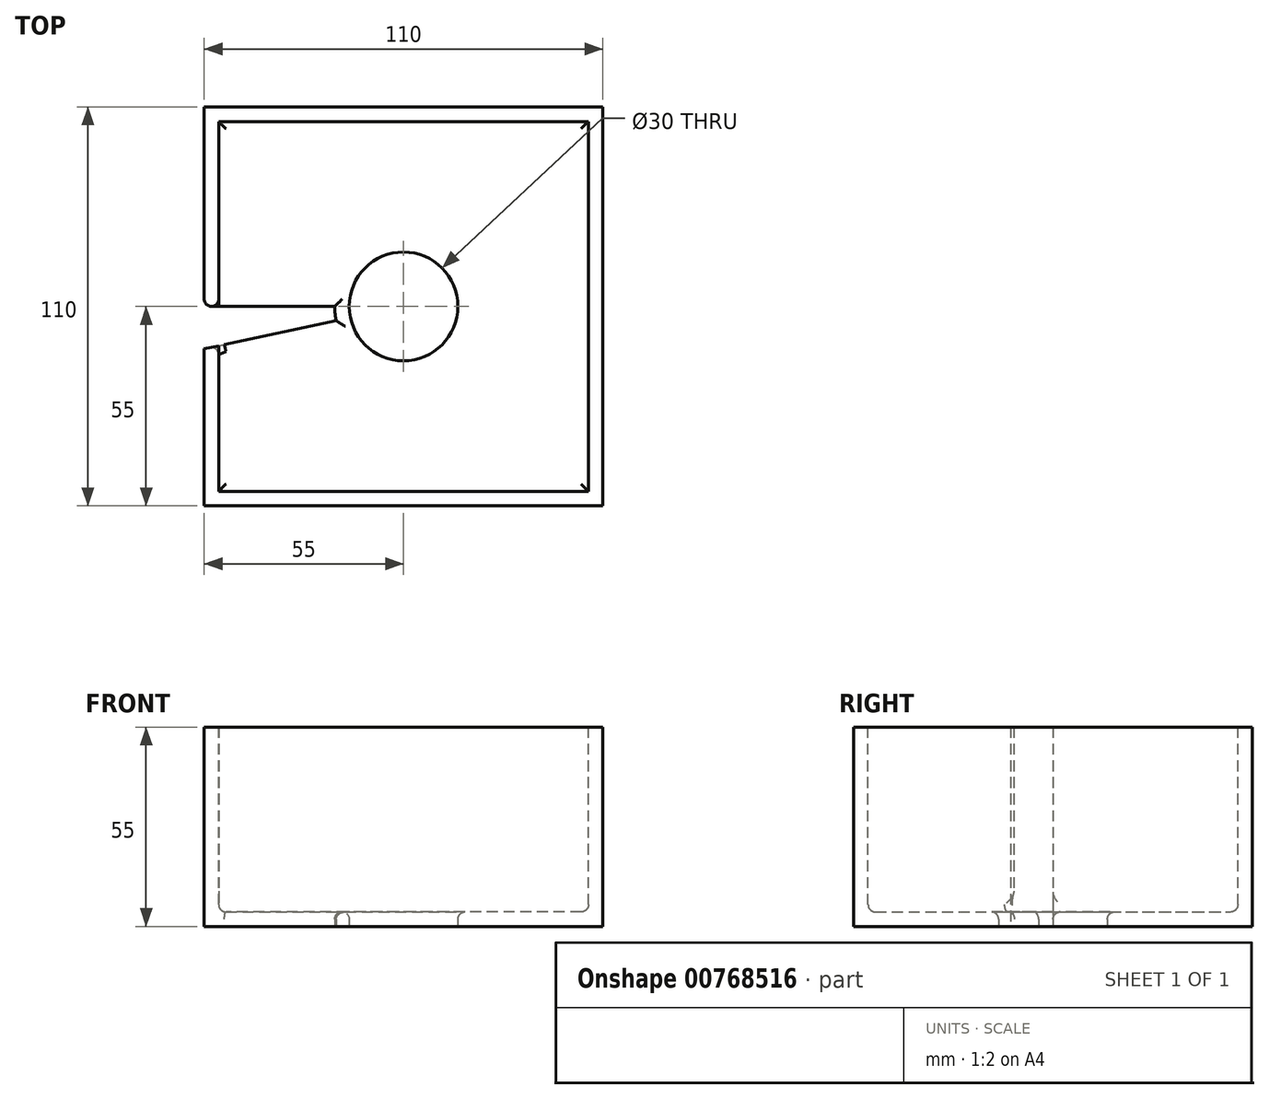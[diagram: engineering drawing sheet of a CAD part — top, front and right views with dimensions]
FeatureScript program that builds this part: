
annotation { "Feature Type Name" : "Feature", "Feature Type Description" : "" }
export const myFeature = defineFeature(function(context is Context, id is Id, definition is map)
    precondition{}
    {
        {
            var Q0;
            Q0=qCreatedBy(makeId("Top.planeOp"),FACE);
            var sketch = newSketch(context, id + "F0", { "sketchPlane" : qUnion([Q0])});
            skLineSegment(sketch, "E0.bottom", {"start": v(55, 55) * mm, "end": v(-55, 55) * mm});
            skLineSegment(sketch, "E0.top", {"start": v(55, -55) * mm, "end": v(-55, -55) * mm});
            skLineSegment(sketch, "E0.left", {"start": v(55, 55) * mm, "end": v(55, -55) * mm});
            skLineSegment(sketch, "E0.right", {"start": v(-55, 55) * mm, "end": v(-55, -55) * mm});
            skPoint(sketch, "E0.middle", {"position": v(0, 0) * mm});
            skSolve(sketch);
        }
        {
            var Q0;
            Q0 = qSketchRegion(id + "F0", true);
            extrude(context, id + "F1", {"entities" : qUnion([Q0]), "depth" : (110 / 2) * mm, "offsetDistance" : 25 * mm});
        }
        {
            var Q0;
            Q0=makeQuery(id+"F1.opExtrude","CAP_FACE",FACE,{"disambiguationData":[OSD([sQuery(id+"F0.wireOp",EDGE,"E0.bottom"),sQuery(id+"F0.wireOp",EDGE,"E0.top"),sQuery(id+"F0.wireOp",EDGE,"E0.left"),sQuery(id+"F0.wireOp",EDGE,"E0.right")])],"isStart":false});
            var sketch = newSketch(context, id + "F2", { "sketchPlane" : qUnion([Q0])});
            skLineSegment(sketch, "E1.bottom", {"start": v(51, -51) * mm, "end": v(-51, -51) * mm});
            skLineSegment(sketch, "E1.top", {"start": v(51, 51) * mm, "end": v(-51, 51) * mm});
            skLineSegment(sketch, "E1.left", {"start": v(51, -51) * mm, "end": v(51, 51) * mm});
            skLineSegment(sketch, "E1.right", {"start": v(-51, -51) * mm, "end": v(-51, 51) * mm});
            skPoint(sketch, "E1.middle", {"position": v(0, 0) * mm});
            skSolve(sketch);
        }
        {
            var Q0;
            Q0 = qSketchRegion(id + "F2", true);
            extrude(context, id + "F3", {"entities" : qUnion([Q0]), "operationType" : NewBodyOperationType.REMOVE, "oppositeDirection" : true, "depth" : ((110 / 2) - 4) * mm, "offsetDistance" : 25 * mm});
        }
        {
            var Q0;
            Q0=makeQuery(id+"F1.opExtrude","CAP_FACE",FACE,{"disambiguationData":[OSD([sQuery(id+"F0.wireOp",EDGE,"E0.bottom"),sQuery(id+"F0.wireOp",EDGE,"E0.top"),sQuery(id+"F0.wireOp",EDGE,"E0.left"),sQuery(id+"F0.wireOp",EDGE,"E0.right")])],"isStart":true});
            var sketch = newSketch(context, id + "F4", { "sketchPlane" : qUnion([Q0])});
            skPoint(sketch, "E2.endSnap0", {"position": v(-55, 0) * mm});
            skLineSegment(sketch, "E3", {"start": v(-19, 0) * mm, "end": v(-85, 0) * mm});
            skLineSegment(sketch, "E4", {"start": v(-18.58, 3.95) * mm, "end": v(-83.14, 17.67) * mm});
            skArc(sketch, "E5", {"start": v(-19, 0) * mm, "mid": v(-18.9, 1.99) * mm, "end": v(-18.58, 3.95) * mm});
            skArc(sketch, "E6", {"start": v(-85, 0) * mm, "mid": v(-84.53, 8.88) * mm, "end": v(-83.14, 17.67) * mm});
            skSolve(sketch);
        }
        {
            var Q0;
            Q0 = qSketchRegion(id + "F4", true);
            extrude(context, id + "F5", {"entities" : qUnion([Q0]), "operationType" : NewBodyOperationType.REMOVE, "endBound" : BoundingType.THROUGH_ALL, "oppositeDirection" : true, "depth" : 25 * mm, "offsetDistance" : 25 * mm});
        }
        {
            var Q0;
            Q0=qCreatedBy(makeId("Right.planeOp"),FACE);
            var sketch = newSketch(context, id + "F6", { "sketchPlane" : qUnion([Q0])});
            skLineSegment(sketch, "E7", {"start": v(0, -32.4) * mm, "end": v(0, 66.47) * mm});
            skSolve(sketch);
        }
        {
            var Q0;
            Q0=makeQuery(id+"F1.opExtrude","CAP_FACE",FACE,{"disambiguationData":[OSD([sQuery(id+"F0.wireOp",EDGE,"E0.bottom"),sQuery(id+"F0.wireOp",EDGE,"E0.top"),sQuery(id+"F0.wireOp",EDGE,"E0.left"),sQuery(id+"F0.wireOp",EDGE,"E0.right")])],"isStart":true});
            var sketch = newSketch(context, id + "F7", { "sketchPlane" : qUnion([Q0])});
            skCircle(sketch, "E8", {"center": v(0, 0) * mm, "radius": 15 * mm});
            skSolve(sketch);
        }
        {
            var Q0;
            Q0 = qSketchRegion(id + "F7", true);
            extrude(context, id + "F8", {"entities" : qUnion([Q0]), "operationType" : NewBodyOperationType.REMOVE, "endBound" : BoundingType.THROUGH_ALL, "oppositeDirection" : true, "depth" : 25 * mm, "offsetDistance" : 25 * mm});
        }
        {
            var Q0;
            Q0=makeQuery(id+"Fbr1V4HkgtgxKTV_1.12.F5.boolean.opBoolean","INTERSECT",EDGE,{"derivedFrom":[makeQuery(id+"F3.boolean.opBoolean","COPY",FACE,{"derivedFrom":makeQuery(id+"F3.opExtrude","CAP_FACE",FACE,{"disambiguationData":[OSD([sQuery(id+"F2.wireOp",EDGE,"E1.bottom"),sQuery(id+"F2.wireOp",EDGE,"E1.top"),sQuery(id+"F2.wireOp",EDGE,"E1.left"),sQuery(id+"F2.wireOp",EDGE,"E1.right")])],"isStart":false})}),makeQuery(id+"Fbr1V4HkgtgxKTV_1.12.F5.opExtrude","SWEPT_FACE",FACE,{"disambiguationData":[OSD([sQuery(id+"F4.wireOp",EDGE,"E4")])]})]});
            var Q1;
            Q1=makeQuery(id+"Fbr1V4HkgtgxKTV_1.13.F5.boolean.opBoolean","INTERSECT",EDGE,{"derivedFrom":[makeQuery(id+"F3.boolean.opBoolean","COPY",FACE,{"derivedFrom":makeQuery(id+"F3.opExtrude","CAP_FACE",FACE,{"disambiguationData":[OSD([sQuery(id+"F2.wireOp",EDGE,"E1.bottom"),sQuery(id+"F2.wireOp",EDGE,"E1.top"),sQuery(id+"F2.wireOp",EDGE,"E1.left"),sQuery(id+"F2.wireOp",EDGE,"E1.right")])],"isStart":false})}),makeQuery(id+"Fbr1V4HkgtgxKTV_1.13.F5.opExtrude","SWEPT_FACE",FACE,{"disambiguationData":[OSD([sQuery(id+"F4.wireOp",EDGE,"E3")])]})]});
            var Q2;
            Q2=makeQuery(id+"Fbr1V4HkgtgxKTV_1.13.F5.boolean.opBoolean","INTERSECT",EDGE,{"derivedFrom":[makeQuery(id+"F3.boolean.opBoolean","COPY",FACE,{"derivedFrom":makeQuery(id+"F3.opExtrude","CAP_FACE",FACE,{"disambiguationData":[OSD([sQuery(id+"F2.wireOp",EDGE,"E1.bottom"),sQuery(id+"F2.wireOp",EDGE,"E1.top"),sQuery(id+"F2.wireOp",EDGE,"E1.left"),sQuery(id+"F2.wireOp",EDGE,"E1.right")])],"isStart":false})}),makeQuery(id+"Fbr1V4HkgtgxKTV_1.13.F5.opExtrude","SWEPT_FACE",FACE,{"disambiguationData":[OSD([sQuery(id+"F4.wireOp",EDGE,"E4")])]})]});
            var Q3;
            Q3=makeQuery(id+"F3.boolean.opBoolean","COPY",FACE,{"derivedFrom":makeQuery(id+"F3.opExtrude","CAP_FACE",FACE,{"disambiguationData":[OSD([sQuery(id+"F2.wireOp",EDGE,"E1.bottom"),sQuery(id+"F2.wireOp",EDGE,"E1.top"),sQuery(id+"F2.wireOp",EDGE,"E1.left"),sQuery(id+"F2.wireOp",EDGE,"E1.right")])],"isStart":false})});
            fillet(context, id + "F9", {"entities" : qUnion([Q0, Q1, Q2, Q3]), "radius" : 2 * mm, "tangentPropagation" : true, "allowEdgeOverflow" : false});
        }
        {
            var Q0;
            {var subQ0=sQuery(id+"F0.wireOp",EDGE,"E0.right");var subQ3=sQuery(id+"F0.wireOp",EDGE,"E0.bottom");var subQ6=makeQuery(id+"F1.opExtrude","SWEPT_FACE",FACE,{"disambiguationData":[OSD([subQ0])]});Q0=makeQuery(id+"Fbr1V4HkgtgxKTV_1.12.F5.boolean.opBoolean","INTERSECT",EDGE,{"derivedFrom":[makeQuery(id+"Fbr1V4HkgtgxKTV_1.11.F5.boolean.opBoolean","SPLIT",FACE,{"disambiguationData":[TD([subQ6])],"derivedFrom":makeQuery(id+"Fbr1V4HkgtgxKTV_1.10.F5.boolean.opBoolean","SPLIT",FACE,{"disambiguationData":[TD([subQ6])],"derivedFrom":makeQuery(id+"Fbr1V4HkgtgxKTV_1.9.F5.boolean.opBoolean","SPLIT",FACE,{"disambiguationData":[TD([subQ6])],"derivedFrom":makeQuery(id+"F1.opExtrude","SWEPT_FACE",FACE,{"disambiguationData":[OSD([subQ3])]})})})}),makeQuery(id+"Fbr1V4HkgtgxKTV_1.12.F5.opExtrude","SWEPT_FACE",FACE,{"disambiguationData":[OSD([sQuery(id+"F4.wireOp",EDGE,"E3")])]})]});}
            var Q1;
            {var subQ0=sQuery(id+"F0.wireOp",EDGE,"E0.bottom");var subQ1=sQuery(id+"F0.wireOp",EDGE,"E0.right");Q1=makeQuery(id+"Fbr1V4HkgtgxKTV_1.12.F5.boolean.opBoolean","INTERSECT",EDGE,{"derivedFrom":[makeQuery(id+"F5.boolean.opBoolean","SPLIT",FACE,{"disambiguationData":[TD([makeQuery(id+"F1.opExtrude","SWEPT_FACE",FACE,{"disambiguationData":[OSD([subQ0])]})])],"derivedFrom":makeQuery(id+"F1.opExtrude","SWEPT_FACE",FACE,{"disambiguationData":[OSD([subQ1])]})}),makeQuery(id+"Fbr1V4HkgtgxKTV_1.12.F5.opExtrude","SWEPT_FACE",FACE,{"disambiguationData":[OSD([sQuery(id+"F4.wireOp",EDGE,"E4")])]})]});}
            var Q2;
            {var subQ0=sQuery(id+"F0.wireOp",EDGE,"E0.bottom");var subQ1=sQuery(id+"F0.wireOp",EDGE,"E0.right");Q2=makeQuery(id+"Fbr1V4HkgtgxKTV_1.13.F5.boolean.opBoolean","INTERSECT",EDGE,{"derivedFrom":[makeQuery(id+"F5.boolean.opBoolean","SPLIT",FACE,{"disambiguationData":[TD([makeQuery(id+"F1.opExtrude","SWEPT_FACE",FACE,{"disambiguationData":[OSD([subQ0])]})])],"derivedFrom":makeQuery(id+"F1.opExtrude","SWEPT_FACE",FACE,{"disambiguationData":[OSD([subQ1])]})}),makeQuery(id+"Fbr1V4HkgtgxKTV_1.13.F5.opExtrude","SWEPT_FACE",FACE,{"disambiguationData":[OSD([sQuery(id+"F4.wireOp",EDGE,"E4")])]})]});}
            var Q3;
            {var subQ0=sQuery(id+"F0.wireOp",EDGE,"E0.right");var subQ2=sQuery(id+"F0.wireOp",EDGE,"E0.top");Q3=makeQuery(id+"Fbr1V4HkgtgxKTV_1.1.F5.boolean.opBoolean","INTERSECT",EDGE,{"derivedFrom":[makeQuery(id+"F5.boolean.opBoolean","SPLIT",FACE,{"disambiguationData":[TD([makeQuery(id+"F1.opExtrude","SWEPT_FACE",FACE,{"disambiguationData":[OSD([subQ2])]})])],"derivedFrom":makeQuery(id+"F1.opExtrude","SWEPT_FACE",FACE,{"disambiguationData":[OSD([subQ0])]})}),makeQuery(id+"Fbr1V4HkgtgxKTV_1.1.F5.opExtrude","SWEPT_FACE",FACE,{"disambiguationData":[OSD([sQuery(id+"F4.wireOp",EDGE,"E3")])]})]});}
            var Q4;
            Q4=makeQuery(id+"Fbr1V4HkgtgxKTV_1.2.F5.boolean.opBoolean","INTERSECT",EDGE,{"derivedFrom":[makeQuery(id+"F1.opExtrude","SWEPT_FACE",FACE,{"disambiguationData":[OSD([sQuery(id+"F0.wireOp",EDGE,"E0.top")])]}),makeQuery(id+"Fbr1V4HkgtgxKTV_1.2.F5.opExtrude","SWEPT_FACE",FACE,{"disambiguationData":[OSD([sQuery(id+"F4.wireOp",EDGE,"E4")])]})]});
            var Q5;
            {var subQ1=sQuery(id+"F0.wireOp",EDGE,"E0.left");var subQ2=sQuery(id+"F0.wireOp",EDGE,"E0.top");var subQ7=makeQuery(id+"F1.opExtrude","SWEPT_FACE",FACE,{"disambiguationData":[OSD([subQ1])]});Q5=makeQuery(id+"Fbr1V4HkgtgxKTV_1.4.F5.boolean.opBoolean","INTERSECT",EDGE,{"derivedFrom":[makeQuery(id+"Fbr1V4HkgtgxKTV_1.3.F5.boolean.opBoolean","SPLIT",FACE,{"disambiguationData":[TD([subQ7])],"derivedFrom":makeQuery(id+"Fbr1V4HkgtgxKTV_1.2.F5.boolean.opBoolean","SPLIT",FACE,{"disambiguationData":[TD([subQ7])],"derivedFrom":makeQuery(id+"F1.opExtrude","SWEPT_FACE",FACE,{"disambiguationData":[OSD([subQ2])]})})}),makeQuery(id+"Fbr1V4HkgtgxKTV_1.4.F5.opExtrude","SWEPT_FACE",FACE,{"disambiguationData":[OSD([sQuery(id+"F4.wireOp",EDGE,"E3")])]})]});}
            var Q6;
            {var subQ1=sQuery(id+"F0.wireOp",EDGE,"E0.left");var subQ2=sQuery(id+"F0.wireOp",EDGE,"E0.top");var subQ6=makeQuery(id+"F1.opExtrude","SWEPT_FACE",FACE,{"disambiguationData":[OSD([subQ1])]});Q6=makeQuery(id+"Fbr1V4HkgtgxKTV_1.5.F5.boolean.opBoolean","INTERSECT",EDGE,{"derivedFrom":[makeQuery(id+"Fbr1V4HkgtgxKTV_1.4.F5.boolean.opBoolean","SPLIT",FACE,{"disambiguationData":[TD([subQ6])],"derivedFrom":makeQuery(id+"Fbr1V4HkgtgxKTV_1.3.F5.boolean.opBoolean","SPLIT",FACE,{"disambiguationData":[TD([subQ6])],"derivedFrom":makeQuery(id+"Fbr1V4HkgtgxKTV_1.2.F5.boolean.opBoolean","SPLIT",FACE,{"disambiguationData":[TD([subQ6])],"derivedFrom":makeQuery(id+"F1.opExtrude","SWEPT_FACE",FACE,{"disambiguationData":[OSD([subQ2])]})})})}),makeQuery(id+"Fbr1V4HkgtgxKTV_1.5.F5.opExtrude","SWEPT_FACE",FACE,{"disambiguationData":[OSD([sQuery(id+"F4.wireOp",EDGE,"E3")])]})]});}
            var Q7;
            Q7=makeQuery(id+"Fbr1V4HkgtgxKTV_1.5.F5.boolean.opBoolean","INTERSECT",EDGE,{"derivedFrom":[makeQuery(id+"F1.opExtrude","SWEPT_FACE",FACE,{"disambiguationData":[OSD([sQuery(id+"F0.wireOp",EDGE,"E0.left")])]}),makeQuery(id+"Fbr1V4HkgtgxKTV_1.5.F5.opExtrude","SWEPT_FACE",FACE,{"disambiguationData":[OSD([sQuery(id+"F4.wireOp",EDGE,"E4")])]})]});
            var Q8;
            Q8=makeQuery(id+"Fbr1V4HkgtgxKTV_1.6.F5.boolean.opBoolean","INTERSECT",EDGE,{"derivedFrom":[makeQuery(id+"F1.opExtrude","SWEPT_FACE",FACE,{"disambiguationData":[OSD([sQuery(id+"F0.wireOp",EDGE,"E0.left")])]}),makeQuery(id+"Fbr1V4HkgtgxKTV_1.6.F5.opExtrude","SWEPT_FACE",FACE,{"disambiguationData":[OSD([sQuery(id+"F4.wireOp",EDGE,"E4")])]})]});
            var Q9;
            {var subQ0=sQuery(id+"F0.wireOp",EDGE,"E0.bottom");var subQ2=sQuery(id+"F0.wireOp",EDGE,"E0.left");Q9=makeQuery(id+"Fbr1V4HkgtgxKTV_1.7.F5.boolean.opBoolean","INTERSECT",EDGE,{"derivedFrom":[makeQuery(id+"Fbr1V4HkgtgxKTV_1.6.F5.boolean.opBoolean","SPLIT",FACE,{"disambiguationData":[TD([makeQuery(id+"F1.opExtrude","SWEPT_FACE",FACE,{"disambiguationData":[OSD([subQ0])]})])],"derivedFrom":makeQuery(id+"F1.opExtrude","SWEPT_FACE",FACE,{"disambiguationData":[OSD([subQ2])]})}),makeQuery(id+"Fbr1V4HkgtgxKTV_1.7.F5.opExtrude","SWEPT_FACE",FACE,{"disambiguationData":[OSD([sQuery(id+"F4.wireOp",EDGE,"E3")])]})]});}
            var Q10;
            {var subQ0=sQuery(id+"F4.wireOp",EDGE,"E4");var subQ1=sQuery(id+"F0.wireOp",EDGE,"E0.bottom");var subQ3=sQuery(id+"F0.wireOp",EDGE,"E0.left");Q10=makeQuery(id+"Fbr1V4HkgtgxKTV_1.7.F5.boolean.opBoolean","INTERSECT",EDGE,{"derivedFrom":[makeQuery(id+"Fbr1V4HkgtgxKTV_1.6.F5.boolean.opBoolean","SPLIT",FACE,{"disambiguationData":[TD([makeQuery(id+"F1.opExtrude","SWEPT_FACE",FACE,{"disambiguationData":[OSD([subQ1])]})])],"derivedFrom":makeQuery(id+"F1.opExtrude","SWEPT_FACE",FACE,{"disambiguationData":[OSD([subQ3])]})}),makeQuery(id+"Fbr1V4HkgtgxKTV_1.7.F5.opExtrude","SWEPT_FACE",FACE,{"disambiguationData":[OSD([subQ0])]})]});}
            var Q11;
            {var subQ0=sQuery(id+"F0.wireOp",EDGE,"E0.bottom");var subQ1=makeQuery(id+"F1.opExtrude","SWEPT_FACE",FACE,{"disambiguationData":[OSD([subQ0])]});var subQ4=sQuery(id+"F0.wireOp",EDGE,"E0.left");Q11=makeQuery(id+"Fbr1V4HkgtgxKTV_1.8.F5.boolean.opBoolean","INTERSECT",EDGE,{"derivedFrom":[makeQuery(id+"Fbr1V4HkgtgxKTV_1.7.F5.boolean.opBoolean","SPLIT",FACE,{"disambiguationData":[TD([subQ1])],"derivedFrom":makeQuery(id+"Fbr1V4HkgtgxKTV_1.6.F5.boolean.opBoolean","SPLIT",FACE,{"disambiguationData":[TD([subQ1])],"derivedFrom":makeQuery(id+"F1.opExtrude","SWEPT_FACE",FACE,{"disambiguationData":[OSD([subQ4])]})})}),makeQuery(id+"Fbr1V4HkgtgxKTV_1.8.F5.opExtrude","SWEPT_FACE",FACE,{"disambiguationData":[OSD([sQuery(id+"F4.wireOp",EDGE,"E3")])]})]});}
            var Q12;
            Q12=makeQuery(id+"Fbr1V4HkgtgxKTV_1.9.F5.boolean.opBoolean","INTERSECT",EDGE,{"derivedFrom":[makeQuery(id+"F1.opExtrude","SWEPT_FACE",FACE,{"disambiguationData":[OSD([sQuery(id+"F0.wireOp",EDGE,"E0.bottom")])]}),makeQuery(id+"Fbr1V4HkgtgxKTV_1.9.F5.opExtrude","SWEPT_FACE",FACE,{"disambiguationData":[OSD([sQuery(id+"F4.wireOp",EDGE,"E4")])]})]});
            var Q13;
            {var subQ0=sQuery(id+"F0.wireOp",EDGE,"E0.right");var subQ3=sQuery(id+"F0.wireOp",EDGE,"E0.bottom");Q13=makeQuery(id+"Fbr1V4HkgtgxKTV_1.10.F5.boolean.opBoolean","INTERSECT",EDGE,{"derivedFrom":[makeQuery(id+"Fbr1V4HkgtgxKTV_1.9.F5.boolean.opBoolean","SPLIT",FACE,{"disambiguationData":[TD([makeQuery(id+"F1.opExtrude","SWEPT_FACE",FACE,{"disambiguationData":[OSD([subQ0])]})])],"derivedFrom":makeQuery(id+"F1.opExtrude","SWEPT_FACE",FACE,{"disambiguationData":[OSD([subQ3])]})}),makeQuery(id+"Fbr1V4HkgtgxKTV_1.10.F5.opExtrude","SWEPT_FACE",FACE,{"disambiguationData":[OSD([sQuery(id+"F4.wireOp",EDGE,"E3")])]})]});}
            var Q14;
            {var subQ0=sQuery(id+"F4.wireOp",EDGE,"E4");var subQ1=sQuery(id+"F0.wireOp",EDGE,"E0.right");var subQ4=sQuery(id+"F0.wireOp",EDGE,"E0.bottom");Q14=makeQuery(id+"Fbr1V4HkgtgxKTV_1.10.F5.boolean.opBoolean","INTERSECT",EDGE,{"derivedFrom":[makeQuery(id+"Fbr1V4HkgtgxKTV_1.9.F5.boolean.opBoolean","SPLIT",FACE,{"disambiguationData":[TD([makeQuery(id+"F1.opExtrude","SWEPT_FACE",FACE,{"disambiguationData":[OSD([subQ1])]})])],"derivedFrom":makeQuery(id+"F1.opExtrude","SWEPT_FACE",FACE,{"disambiguationData":[OSD([subQ4])]})}),makeQuery(id+"Fbr1V4HkgtgxKTV_1.10.F5.opExtrude","SWEPT_FACE",FACE,{"disambiguationData":[OSD([subQ0])]})]});}
            var Q15;
            Q15=makeQuery(id+"F5.boolean.opBoolean","INTERSECT",EDGE,{"derivedFrom":[makeQuery(id+"F1.opExtrude","SWEPT_FACE",FACE,{"disambiguationData":[OSD([sQuery(id+"F0.wireOp",EDGE,"E0.right")])]}),makeQuery(id+"F5.opExtrude","SWEPT_FACE",FACE,{"disambiguationData":[OSD([sQuery(id+"F4.wireOp",EDGE,"E3")])]})]});
            fillet(context, id + "F10", {"entities" : qUnion([Q0, Q1, Q2, Q3, Q4, Q5, Q6, Q7, Q8, Q9, Q10, Q11, Q12, Q13, Q14, Q15]), "radius" : 2 * mm, "tangentPropagation" : true, "allowEdgeOverflow" : false});
        }
    });
